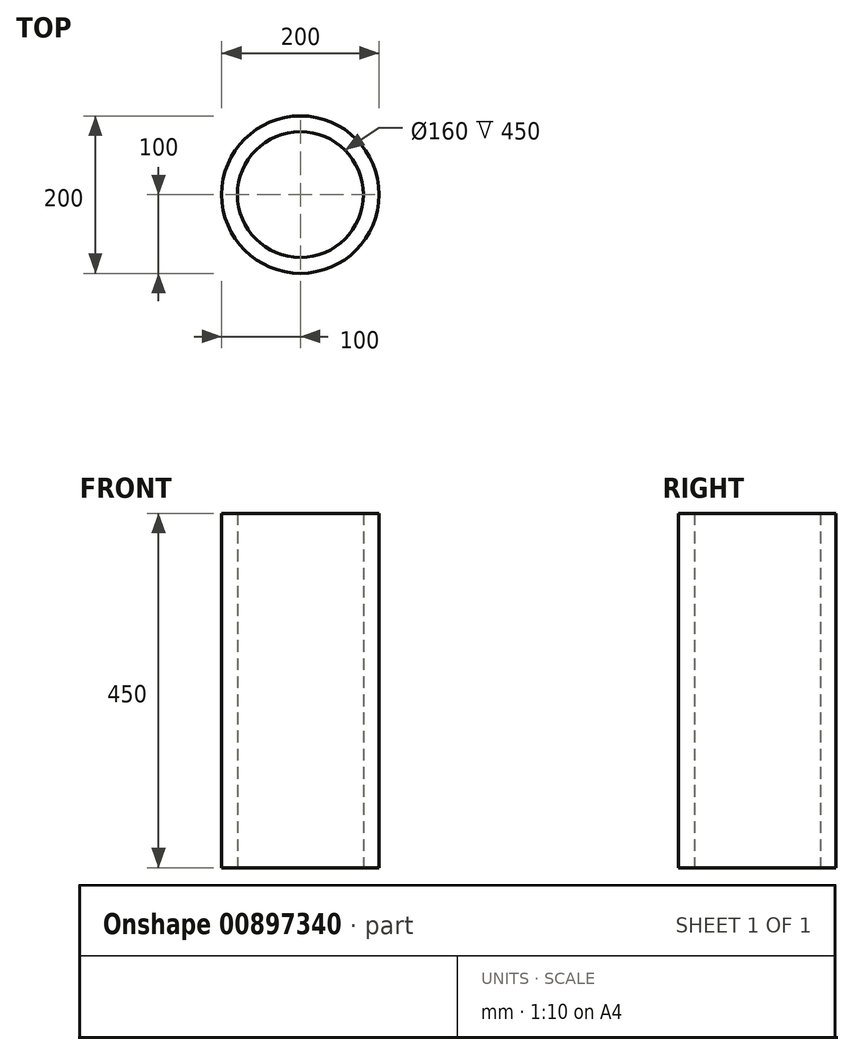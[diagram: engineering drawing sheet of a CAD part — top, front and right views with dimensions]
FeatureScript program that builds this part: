
annotation { "Feature Type Name" : "Feature", "Feature Type Description" : "" }
export const myFeature = defineFeature(function(context is Context, id is Id, definition is map)
    precondition{}
    {
        {
            var Q0;
            Q0=qCreatedBy(makeId("Top.planeOp"),FACE);
            var sketch = newSketch(context, id + "F0", { "sketchPlane" : qUnion([Q0])});
            skCircle(sketch, "E0", {"center": v(0, 0) * mm, "radius": 80 * mm});
            skCircle(sketch, "E1.0", {"center": v(0, 0) * mm, "radius": 100 * mm});
            skSolve(sketch);
        }
        {
            var Q0;
            Q0=makeQuery(id+"F0.imprint","IMPRINT",FACE,{"disambiguationData":[TD([[makeQuery(id+"F0.imprint","IMPRINT",EDGE,{"derivedFrom":sQuery(id+"F0.wireOp",EDGE,"E0")}),-1.0]])]});
            extrude(context, id + "F1", {"entities" : qUnion([Q0]), "depth" : 450 * mm, "offsetDistance" : 25 * mm});
        }
    });
